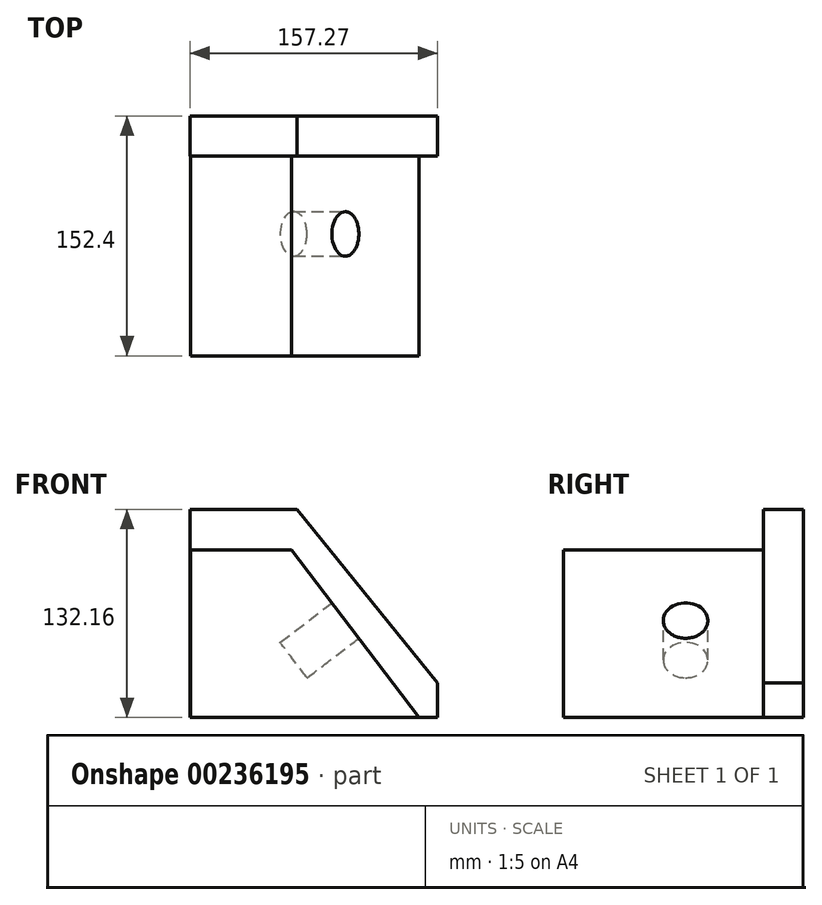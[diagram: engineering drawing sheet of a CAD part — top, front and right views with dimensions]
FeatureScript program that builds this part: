
annotation { "Feature Type Name" : "Feature", "Feature Type Description" : "" }
export const myFeature = defineFeature(function(context is Context, id is Id, definition is map)
    precondition{}
    {
        {
            var Q0;
            Q0=qCreatedBy(makeId("Front.planeOp"),FACE);
            var sketch = newSketch(context, id + "F0", { "sketchPlane" : qUnion([Q0])});
            skLineSegment(sketch, "E0.bottom", {"start": v(-57.66, 50.37) * mm, "end": v(87.62, 50.37) * mm});
            skLineSegment(sketch, "E0.top", {"start": v(-57.66, -56.04) * mm, "end": v(87.62, -56.04) * mm});
            skLineSegment(sketch, "E0.left", {"start": v(-57.66, 50.37) * mm, "end": v(-57.66, -56.04) * mm});
            skLineSegment(sketch, "E0.right", {"start": v(87.62, 50.37) * mm, "end": v(87.62, -56.04) * mm});
            skSolve(sketch);
        }
        {
            var Q0;
            Q0=makeQuery(id+"F0.imprint","IMPRINT",FACE,{"disambiguationData":[TD([[makeQuery(id+"F0.imprint","IMPRINT",EDGE,{"derivedFrom":sQuery(id+"F0.wireOp",EDGE,"E0.bottom")}),-1.0]])]});
            extrude(context, id + "F1", {"entities" : qUnion([Q0]), "depth" : 152.4 * mm});
        }
        {
            var Q0;
            Q0=qCreatedBy(makeId("Front.planeOp"),FACE);
            var sketch = newSketch(context, id + "F2", { "sketchPlane" : qUnion([Q0])});
            skLineSegment(sketch, "E1", {"start": v(0, 58.91) * mm, "end": v(91.32, -60.74) * mm});
            skLineSegment(sketch, "E2", {"start": v(91.32, -60.74) * mm, "end": v(91.32, 59.44) * mm});
            skLineSegment(sketch, "E3", {"start": v(91.32, 59.44) * mm, "end": v(0, 58.91) * mm});
            skSolve(sketch);
        }
        {
            var Q0;
            Q0 = qSketchRegion(id + "F2", true);
            extrude(context, id + "F3", {"entities" : qUnion([Q0]), "operationType" : NewBodyOperationType.REMOVE, "oppositeDirection" : true, "depth" : 25.4 * mm, "hasSecondDirection" : true, "secondDirectionOppositeDirection" : false, "secondDirectionDepth" : 193.04 * mm});
        }
        {
            var Q0;
            Q0=makeQuery(id+"F3.boolean.opBoolean","COPY",FACE,{"derivedFrom":makeQuery(id+"F3.opExtrude","SWEPT_FACE",FACE,{"disambiguationData":[OSD([sQuery(id+"F2.wireOp",EDGE,"E1")])]})});
            var sketch = newSketch(context, id + "F4", { "sketchPlane" : qUnion([Q0])});
            skCircle(sketch, "E4", {"center": v(-74.89, -20.33) * mm, "radius": 14.14 * mm});
            skSolve(sketch);
        }
        {
            var Q0;
            Q0 = qSketchRegion(id + "F4", true);
            extrude(context, id + "F5", {"entities" : qUnion([Q0]), "operationType" : NewBodyOperationType.REMOVE, "oppositeDirection" : true, "depth" : 41.4 * mm});
        }
        {
            var Q0;
            Q0=qCreatedBy(makeId("Front.planeOp"),FACE);
            var sketch = newSketch(context, id + "F6", { "sketchPlane" : qUnion([Q0])});
            skLineSegment(sketch, "E5.bottom", {"start": v(-57.94, 76.12) * mm, "end": v(9.92, 76.12) * mm});
            skLineSegment(sketch, "E5.top", {"start": v(-57.94, -56.04) * mm, "end": v(99.33, -56.04) * mm});
            skLineSegment(sketch, "E5.left", {"start": v(-57.94, 76.12) * mm, "end": v(-57.94, -56.04) * mm});
            skLineSegment(sketch, "E5.right", {"start": v(99.33, -34.17) * mm, "end": v(99.33, -56.04) * mm});
            skLineSegment(sketch, "E6", {"start": v(9.92, 76.12) * mm, "end": v(99.33, -34.17) * mm});
            skSolve(sketch);
        }
        {
            var Q0;
            Q0 = qSketchRegion(id + "F6", true);
            extrude(context, id + "F7", {"entities" : qUnion([Q0]), "operationType" : NewBodyOperationType.ADD, "depth" : 25.4 * mm});
        }
    });
